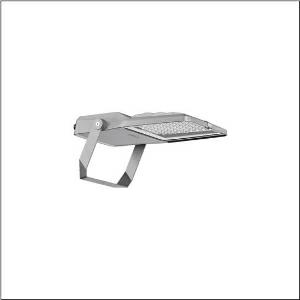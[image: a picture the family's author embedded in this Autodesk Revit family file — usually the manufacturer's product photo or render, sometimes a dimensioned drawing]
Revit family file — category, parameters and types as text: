
# Revit family: floodlight_fl_21_iq_mini___rs12_5xa7772c2b1a_7425
name_source: partatom
category: Lighting Fixtures
units: mm (PartAtom-declared; Revit-internal decimal feet)

## family parameters
Cut with Voids When Loaded = No
Host = Face
Light Source = No
Part Type = Normal
Room Calculation Point = No
Round Connector Dimension = Use Diameter
Shared = No

## types (1)
- --- (1 x LED, 12340 lm, 87.2 W, 3000K)
    Apparent Load = 87 VA
    CIE Flux Codes = 79 92 99 100 100
    Color Rendering = 70
    Color Temperature = 3000K
    Default Elevation = 1800 mm
    Description = Floodlight FL 21 iQ mini, floodlight, primary light control with lens, of PMMA, primary optical cover: protective disc, of toughened safety glass, transparent, light distribution: RS12, light emission: direct distribution, installation type: surface-mounted, lamps: LED, High Power LED, rated values: 12.340lm | 87,2W | 141,5lm/W (begin service life); end service life: 12.340lm | 92,1W; at 50% lumin. flux: 6.170lm | 40,1W | 153,9lm/W, colour temperature: 3000K, colour rendering: CRI > 70, light colour: 730, light setting 1 begin service life: 100% | 12.340lm | 87,2W | 141,5lm/W | 3.000K, light setting 1 end service life: 92,1W, further light settings possible, control: Street-Remote, Auto-Match, Temp-Guard, Night-Set, Smart-Wire, Desk-Remote (wireless, voltage-free reading and setting of iQ features in the workshop via application-optimized NFC function/RFID function), optimised constant luminous flux control (CLO 2.0), pre-setting: linear dimming characteristic, with terminal, 6-pole, mains connection: 220..240V, AC, 50/60Hz, luminaire housing, of diecast aluminium, powder-coated, SITECO metallic grey (DB 702S), corrosivity category C5 mid according to DIN EN ISO 12944suitable for swimming poolschlorine-resistant, sealing non-destructively replaceable, mounting bracket, of steel, galvanised, powder-coated, SITECO metallic grey (DB 702S), protection rating (complete): IP66, insulation class (complete): insulation class II (safety insulation), certification: CE, ENEC, VDE, protection symbol: D, impact resistance: IK08, permissible operating ambient temperature: -40..+40°C, permissible operating ambient temperature for outdoor applications: -40..+50°C, standard: DIN EN 12944, LABS conformity tested according to VDMA 24364:2018-05, packaging unit: 1 piece

Light Distribution: RS12
    Height = 70 mm
    Lamp = 1 x LED
    Lamp Light Flux = 12340 lm
    Lamp Power = 87.2 W
    Lamp count = 1
    Length = 485 mm
    Luminous efficacy = 142 lm/W
    Manufacturer = Siteco
    ModVariant = No
    Model = 5XA7772C2B1A
    Number of Poles = 1
    OnlyDefault = Yes
    Power Factor = 1
    Product Name = Floodlight FL 21 iQ mini | RS12
    Product group = floodlight | pylon annexe
    ProductGroupID = 6201
    Protection Class = Protection class II
    Protection Degree = IP 66
    RLX_Detail_Level = 1
    RLX_Emergency_Light_Flux = 0 lm
    RLX_Emergency_Type = 0
    RLX_Emergency_Type_DB = No
    RlxData = <blob elided: 91129 chars, md5=c93110a2>
    Socket = socket
    Standby Power = 0 W
    System Light Flux = 12340 lm
    System Power = 87 W
    Type Comments = factory setting: luminous flux: 100 % | dim-lin: 254 | 456 mA
    Type Image = l_1006845.jpg
    URL = http://relux.com
    VarID = @adj_167113
    Voltage = 0 V
    Weight = 0.00 kg
    Width = 337 mm

## geometry (parser evidence)
native form markers: Blend x4, Sweep x15
no freeform markers — native parametric forms only
